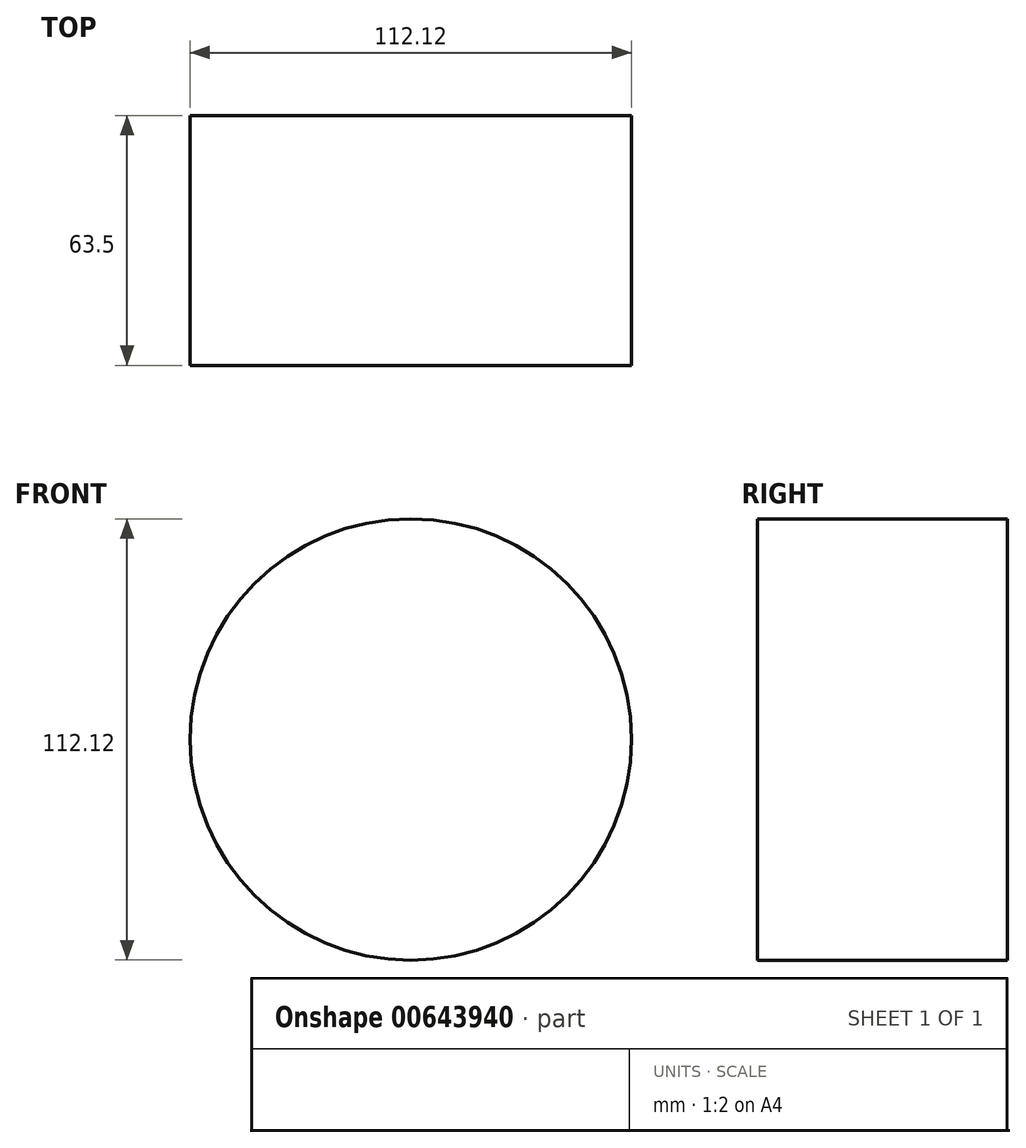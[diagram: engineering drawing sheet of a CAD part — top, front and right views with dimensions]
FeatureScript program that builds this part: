
annotation { "Feature Type Name" : "Feature", "Feature Type Description" : "" }
export const myFeature = defineFeature(function(context is Context, id is Id, definition is map)
    precondition{}
    {
        {
            var Q0;
            Q0=qCreatedBy(makeId("Front.planeOp"),FACE);
            var sketch = newSketch(context, id + "F0", { "sketchPlane" : qUnion([Q0])});
            skCircle(sketch, "E0", {"center": v(0, 0) * mm, "radius": 56.06 * mm});
            skSolve(sketch);
        }
        {
            var Q0;
            Q0 = qSketchRegion(id + "F0", true);
            extrude(context, id + "F1", {"entities" : qUnion([Q0]), "depth" : 63.5 * mm, "offsetDistance" : 25.4 * mm});
        }
    });
